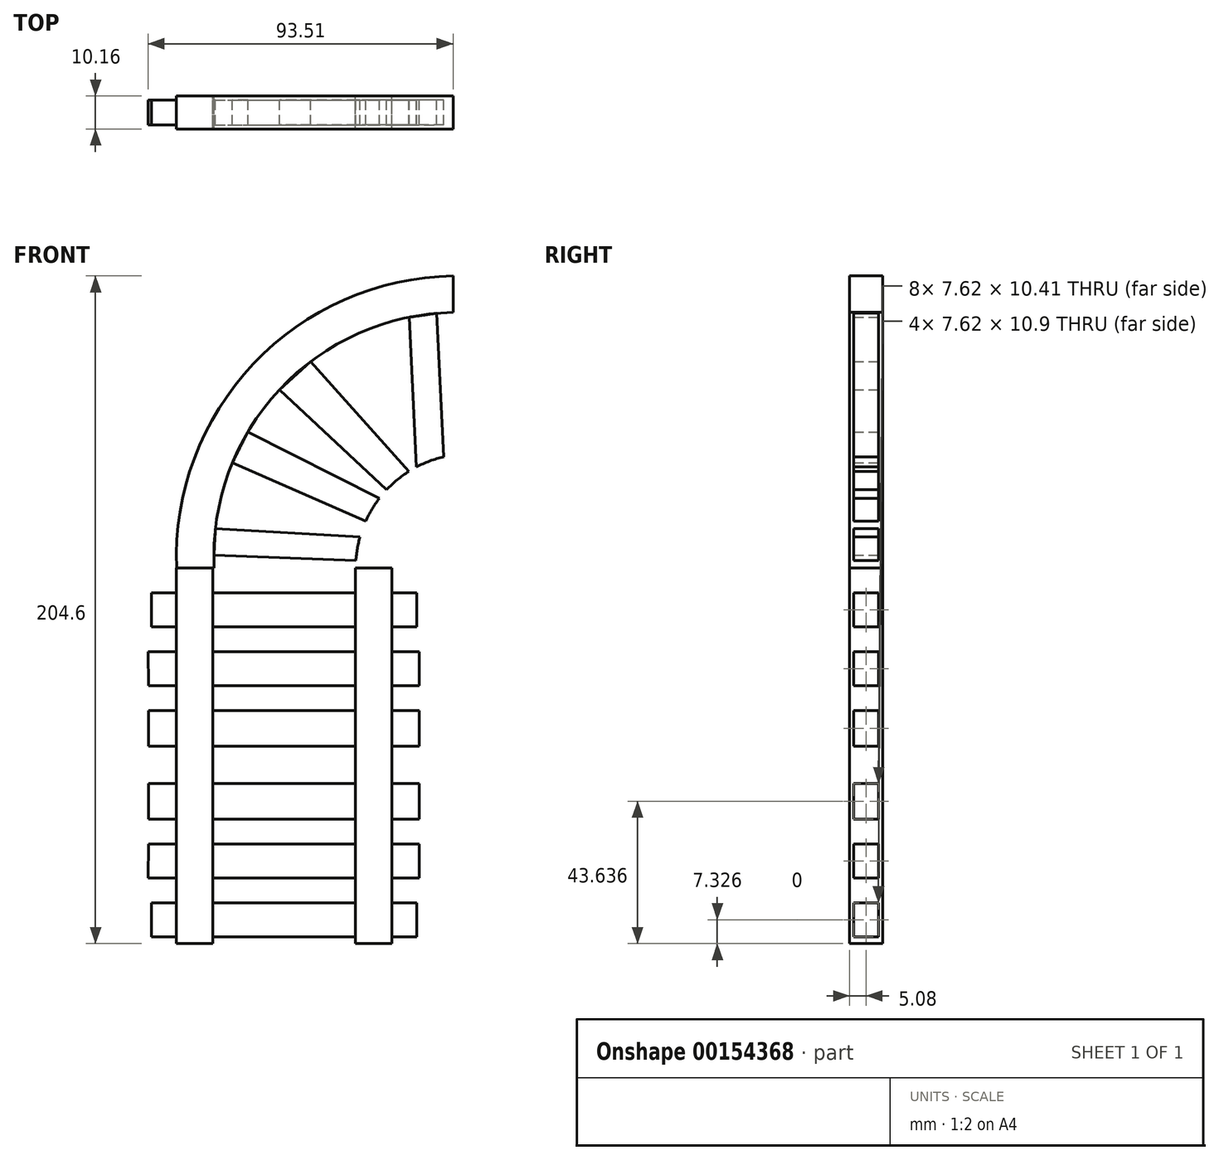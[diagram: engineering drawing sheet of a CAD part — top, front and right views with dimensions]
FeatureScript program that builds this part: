
annotation { "Feature Type Name" : "Feature", "Feature Type Description" : "" }
export const myFeature = defineFeature(function(context is Context, id is Id, definition is map)
    precondition{}
    {
        {
            var Q0;
            Q0=qCreatedBy(makeId("Front.planeOp"),FACE);
            var sketch = newSketch(context, id + "F0", { "sketchPlane" : qUnion([Q0])});
            skLineSegment(sketch, "E0", {"start": v(-21.84, 60.28) * mm, "end": v(-21.84, -54.78) * mm});
            skLineSegment(sketch, "E1", {"start": v(-21.84, -54.78) * mm, "end": v(-33.02, -54.78) * mm});
            skLineSegment(sketch, "E2", {"start": v(-33.02, -54.78) * mm, "end": v(-33.02, 60.28) * mm});
            skLineSegment(sketch, "E3", {"start": v(-33.02, 60.28) * mm, "end": v(-21.84, 60.28) * mm});
            skLineSegment(sketch, "E4.MirrorCS", {"start": v(21.84, 60.28) * mm, "end": v(21.84, -54.78) * mm});
            skLineSegment(sketch, "E5.MirrorCS", {"start": v(33.02, -54.78) * mm, "end": v(33.02, 60.28) * mm});
            skLineSegment(sketch, "E6.MirrorCS", {"start": v(33.02, 60.28) * mm, "end": v(21.84, 60.28) * mm});
            skLineSegment(sketch, "E7.MirrorCS", {"start": v(21.84, -54.78) * mm, "end": v(33.02, -54.78) * mm});
            skLineSegment(sketch, "E8", {"start": v(-40.64, 42.25) * mm, "end": v(40.64, 42.25) * mm});
            skLineSegment(sketch, "E9", {"start": v(40.64, 42.25) * mm, "end": v(40.64, 52.66) * mm});
            skLineSegment(sketch, "E10", {"start": v(40.64, 52.66) * mm, "end": v(-40.64, 52.66) * mm});
            skLineSegment(sketch, "E11", {"start": v(-40.64, 52.66) * mm, "end": v(-40.64, 42.25) * mm});
            skLineSegment(sketch, "E12", {"start": v(-41.74, 34.63) * mm, "end": v(41.35, 34.63) * mm});
            skLineSegment(sketch, "E13", {"start": v(41.35, 34.63) * mm, "end": v(41.35, 24.21) * mm});
            skLineSegment(sketch, "E14", {"start": v(41.35, 24.21) * mm, "end": v(-41.51, 24.21) * mm});
            skLineSegment(sketch, "E15", {"start": v(-41.51, 24.21) * mm, "end": v(-41.74, 34.63) * mm});
            skLineSegment(sketch, "E16", {"start": v(-33.02, 16.6) * mm, "end": v(-41.51, 16.6) * mm});
            skLineSegment(sketch, "E17", {"start": v(-41.51, 16.6) * mm, "end": v(-41.51, 5.7) * mm});
            skLineSegment(sketch, "E18", {"start": v(-41.51, 5.7) * mm, "end": v(41.4, 5.7) * mm});
            skLineSegment(sketch, "E19", {"start": v(41.4, 5.7) * mm, "end": v(41.4, 16.6) * mm});
            skLineSegment(sketch, "E20", {"start": v(-33.02, 16.6) * mm, "end": v(41.4, 16.6) * mm});
            skLineSegment(sketch, "E21.MirrorCS", {"start": v(-41.51, -5.7) * mm, "end": v(41.4, -5.7) * mm});
            skLineSegment(sketch, "E22.MirrorCS", {"start": v(-41.51, -16.6) * mm, "end": v(-41.51, -5.7) * mm});
            skLineSegment(sketch, "E23.MirrorCS", {"start": v(41.4, -5.7) * mm, "end": v(41.4, -16.6) * mm});
            skLineSegment(sketch, "E24.MirrorCS", {"start": v(-33.02, -16.6) * mm, "end": v(41.4, -16.6) * mm});
            skLineSegment(sketch, "E25.MirrorCS", {"start": v(-33.02, -16.6) * mm, "end": v(-41.51, -16.6) * mm});
            skLineSegment(sketch, "E26.MirrorCS", {"start": v(41.35, -24.21) * mm, "end": v(-41.51, -24.21) * mm});
            skLineSegment(sketch, "E27.MirrorCS", {"start": v(-41.74, -34.63) * mm, "end": v(41.35, -34.63) * mm});
            skLineSegment(sketch, "E28.MirrorCS", {"start": v(-41.51, -24.21) * mm, "end": v(-41.74, -34.63) * mm});
            skLineSegment(sketch, "E29.MirrorCS", {"start": v(41.35, -34.63) * mm, "end": v(41.35, -24.21) * mm});
            skLineSegment(sketch, "E30.MirrorCS", {"start": v(40.64, -42.25) * mm, "end": v(40.64, -52.66) * mm});
            skLineSegment(sketch, "E31.MirrorCS", {"start": v(40.64, -52.66) * mm, "end": v(-40.64, -52.66) * mm});
            skLineSegment(sketch, "E32.MirrorCS", {"start": v(-40.64, -42.25) * mm, "end": v(40.64, -42.25) * mm});
            skLineSegment(sketch, "E33.MirrorCS", {"start": v(-40.64, -52.66) * mm, "end": v(-40.64, -42.25) * mm});
            skSolve(sketch);
        }
        {
            var Q0;
            {var subQ0=sQuery(id+"F0.wireOp",EDGE,"E3");Q0=makeQuery(id+"F0.imprint","IMPRINT",FACE,{"disambiguationData":[TD([[makeQuery(id+"F0.imprint","IMPRINT",EDGE,{"derivedFrom":subQ0}),-1.0]])]});}
            var Q1;
            {var subQ0=sQuery(id+"F0.wireOp",EDGE,"E10");var subQ1=sQuery(id+"F0.wireOp",EDGE,"E0");var subQ2=makeQuery(id+"F0.imprint","INTERSECT",VERTEX,{"derivedFrom":[subQ1,subQ0]});Q1=makeQuery(id+"F0.imprint","IMPRINT",FACE,{"disambiguationData":[TD([[makeQuery(id+"F0.imprint","IMPRINT",EDGE,{"disambiguationData":[TD([[subQ2,-1.0]])],"derivedFrom":subQ1}),-1.0]])]});}
            var Q2;
            {var subQ0=sQuery(id+"F0.wireOp",EDGE,"E8");var subQ1=sQuery(id+"F0.wireOp",EDGE,"E0");var subQ2=makeQuery(id+"F0.imprint","INTERSECT",VERTEX,{"derivedFrom":[subQ1,subQ0]});Q2=makeQuery(id+"F0.imprint","IMPRINT",FACE,{"disambiguationData":[TD([[makeQuery(id+"F0.imprint","IMPRINT",EDGE,{"disambiguationData":[TD([[subQ2,-1.0]])],"derivedFrom":subQ1}),-1.0]])]});}
            var Q3;
            {var subQ0=sQuery(id+"F0.wireOp",EDGE,"E12");var subQ1=sQuery(id+"F0.wireOp",EDGE,"E0");var subQ2=makeQuery(id+"F0.imprint","INTERSECT",VERTEX,{"derivedFrom":[subQ1,subQ0]});Q3=makeQuery(id+"F0.imprint","IMPRINT",FACE,{"disambiguationData":[TD([[makeQuery(id+"F0.imprint","IMPRINT",EDGE,{"disambiguationData":[TD([[subQ2,-1.0]])],"derivedFrom":subQ1}),-1.0]])]});}
            var Q4;
            {var subQ0=sQuery(id+"F0.wireOp",EDGE,"E14");var subQ1=sQuery(id+"F0.wireOp",EDGE,"E0");var subQ2=makeQuery(id+"F0.imprint","INTERSECT",VERTEX,{"derivedFrom":[subQ1,subQ0]});Q4=makeQuery(id+"F0.imprint","IMPRINT",FACE,{"disambiguationData":[TD([[makeQuery(id+"F0.imprint","IMPRINT",EDGE,{"disambiguationData":[TD([[subQ2,-1.0]])],"derivedFrom":subQ1}),-1.0]])]});}
            var Q5;
            {var subQ0=sQuery(id+"F0.wireOp",EDGE,"E20");var subQ1=sQuery(id+"F0.wireOp",EDGE,"E0");var subQ2=makeQuery(id+"F0.imprint","INTERSECT",VERTEX,{"derivedFrom":[subQ1,subQ0]});Q5=makeQuery(id+"F0.imprint","IMPRINT",FACE,{"disambiguationData":[TD([[makeQuery(id+"F0.imprint","IMPRINT",EDGE,{"disambiguationData":[TD([[subQ2,-1.0]])],"derivedFrom":subQ1}),-1.0]])]});}
            var Q6;
            {var subQ0=sQuery(id+"F0.wireOp",EDGE,"E18");var subQ1=sQuery(id+"F0.wireOp",EDGE,"E0");var subQ2=makeQuery(id+"F0.imprint","INTERSECT",VERTEX,{"derivedFrom":[subQ1,subQ0]});Q6=makeQuery(id+"F0.imprint","IMPRINT",FACE,{"disambiguationData":[TD([[makeQuery(id+"F0.imprint","IMPRINT",EDGE,{"disambiguationData":[TD([[subQ2,-1.0]])],"derivedFrom":subQ1}),-1.0]])]});}
            var Q7;
            {var subQ0=sQuery(id+"F0.wireOp",EDGE,"E21.MirrorCS");var subQ1=sQuery(id+"F0.wireOp",EDGE,"E0");var subQ2=makeQuery(id+"F0.imprint","INTERSECT",VERTEX,{"derivedFrom":[subQ1,subQ0]});Q7=makeQuery(id+"F0.imprint","IMPRINT",FACE,{"disambiguationData":[TD([[makeQuery(id+"F0.imprint","IMPRINT",EDGE,{"disambiguationData":[TD([[subQ2,-1.0]])],"derivedFrom":subQ1}),-1.0]])]});}
            var Q8;
            {var subQ0=sQuery(id+"F0.wireOp",EDGE,"E24.MirrorCS");var subQ1=sQuery(id+"F0.wireOp",EDGE,"E0");var subQ2=makeQuery(id+"F0.imprint","INTERSECT",VERTEX,{"derivedFrom":[subQ1,subQ0]});Q8=makeQuery(id+"F0.imprint","IMPRINT",FACE,{"disambiguationData":[TD([[makeQuery(id+"F0.imprint","IMPRINT",EDGE,{"disambiguationData":[TD([[subQ2,-1.0]])],"derivedFrom":subQ1}),-1.0]])]});}
            var Q9;
            {var subQ0=sQuery(id+"F0.wireOp",EDGE,"E26.MirrorCS");var subQ1=sQuery(id+"F0.wireOp",EDGE,"E0");var subQ2=makeQuery(id+"F0.imprint","INTERSECT",VERTEX,{"derivedFrom":[subQ1,subQ0]});Q9=makeQuery(id+"F0.imprint","IMPRINT",FACE,{"disambiguationData":[TD([[makeQuery(id+"F0.imprint","IMPRINT",EDGE,{"disambiguationData":[TD([[subQ2,-1.0]])],"derivedFrom":subQ1}),-1.0]])]});}
            var Q10;
            {var subQ0=sQuery(id+"F0.wireOp",EDGE,"E27.MirrorCS");var subQ1=sQuery(id+"F0.wireOp",EDGE,"E0");var subQ2=makeQuery(id+"F0.imprint","INTERSECT",VERTEX,{"derivedFrom":[subQ1,subQ0]});Q10=makeQuery(id+"F0.imprint","IMPRINT",FACE,{"disambiguationData":[TD([[makeQuery(id+"F0.imprint","IMPRINT",EDGE,{"disambiguationData":[TD([[subQ2,-1.0]])],"derivedFrom":subQ1}),-1.0]])]});}
            var Q11;
            {var subQ0=sQuery(id+"F0.wireOp",EDGE,"E31.MirrorCS");var subQ1=sQuery(id+"F0.wireOp",EDGE,"E0");var subQ2=makeQuery(id+"F0.imprint","INTERSECT",VERTEX,{"derivedFrom":[subQ1,subQ0]});Q11=makeQuery(id+"F0.imprint","IMPRINT",FACE,{"disambiguationData":[TD([[makeQuery(id+"F0.imprint","IMPRINT",EDGE,{"disambiguationData":[TD([[subQ2,1.0]])],"derivedFrom":subQ1}),-1.0]])]});}
            var Q12;
            {var subQ0=sQuery(id+"F0.wireOp",EDGE,"E31.MirrorCS");var subQ1=sQuery(id+"F0.wireOp",EDGE,"E4.MirrorCS");var subQ2=makeQuery(id+"F0.imprint","INTERSECT",VERTEX,{"derivedFrom":[subQ1,subQ0]});Q12=makeQuery(id+"F0.imprint","IMPRINT",FACE,{"disambiguationData":[TD([[makeQuery(id+"F0.imprint","IMPRINT",EDGE,{"disambiguationData":[TD([[subQ2,1.0]])],"derivedFrom":subQ1}),1.0]])]});}
            var Q13;
            {var subQ0=sQuery(id+"F0.wireOp",EDGE,"E27.MirrorCS");var subQ1=sQuery(id+"F0.wireOp",EDGE,"E4.MirrorCS");var subQ2=makeQuery(id+"F0.imprint","INTERSECT",VERTEX,{"derivedFrom":[subQ1,subQ0]});Q13=makeQuery(id+"F0.imprint","IMPRINT",FACE,{"disambiguationData":[TD([[makeQuery(id+"F0.imprint","IMPRINT",EDGE,{"disambiguationData":[TD([[subQ2,-1.0]])],"derivedFrom":subQ1}),1.0]])]});}
            var Q14;
            {var subQ0=sQuery(id+"F0.wireOp",EDGE,"E26.MirrorCS");var subQ1=sQuery(id+"F0.wireOp",EDGE,"E4.MirrorCS");var subQ2=makeQuery(id+"F0.imprint","INTERSECT",VERTEX,{"derivedFrom":[subQ1,subQ0]});Q14=makeQuery(id+"F0.imprint","IMPRINT",FACE,{"disambiguationData":[TD([[makeQuery(id+"F0.imprint","IMPRINT",EDGE,{"disambiguationData":[TD([[subQ2,-1.0]])],"derivedFrom":subQ1}),1.0]])]});}
            var Q15;
            {var subQ0=sQuery(id+"F0.wireOp",EDGE,"E24.MirrorCS");var subQ1=sQuery(id+"F0.wireOp",EDGE,"E4.MirrorCS");var subQ2=makeQuery(id+"F0.imprint","INTERSECT",VERTEX,{"derivedFrom":[subQ1,subQ0]});Q15=makeQuery(id+"F0.imprint","IMPRINT",FACE,{"disambiguationData":[TD([[makeQuery(id+"F0.imprint","IMPRINT",EDGE,{"disambiguationData":[TD([[subQ2,-1.0]])],"derivedFrom":subQ1}),1.0]])]});}
            var Q16;
            {var subQ0=sQuery(id+"F0.wireOp",EDGE,"E21.MirrorCS");var subQ1=sQuery(id+"F0.wireOp",EDGE,"E4.MirrorCS");var subQ2=makeQuery(id+"F0.imprint","INTERSECT",VERTEX,{"derivedFrom":[subQ1,subQ0]});Q16=makeQuery(id+"F0.imprint","IMPRINT",FACE,{"disambiguationData":[TD([[makeQuery(id+"F0.imprint","IMPRINT",EDGE,{"disambiguationData":[TD([[subQ2,-1.0]])],"derivedFrom":subQ1}),1.0]])]});}
            var Q17;
            {var subQ0=sQuery(id+"F0.wireOp",EDGE,"E18");var subQ1=sQuery(id+"F0.wireOp",EDGE,"E4.MirrorCS");var subQ2=makeQuery(id+"F0.imprint","INTERSECT",VERTEX,{"derivedFrom":[subQ1,subQ0]});Q17=makeQuery(id+"F0.imprint","IMPRINT",FACE,{"disambiguationData":[TD([[makeQuery(id+"F0.imprint","IMPRINT",EDGE,{"disambiguationData":[TD([[subQ2,-1.0]])],"derivedFrom":subQ1}),1.0]])]});}
            var Q18;
            {var subQ0=sQuery(id+"F0.wireOp",EDGE,"E20");var subQ1=sQuery(id+"F0.wireOp",EDGE,"E4.MirrorCS");var subQ2=makeQuery(id+"F0.imprint","INTERSECT",VERTEX,{"derivedFrom":[subQ1,subQ0]});Q18=makeQuery(id+"F0.imprint","IMPRINT",FACE,{"disambiguationData":[TD([[makeQuery(id+"F0.imprint","IMPRINT",EDGE,{"disambiguationData":[TD([[subQ2,-1.0]])],"derivedFrom":subQ1}),1.0]])]});}
            var Q19;
            {var subQ0=sQuery(id+"F0.wireOp",EDGE,"E14");var subQ1=sQuery(id+"F0.wireOp",EDGE,"E4.MirrorCS");var subQ2=makeQuery(id+"F0.imprint","INTERSECT",VERTEX,{"derivedFrom":[subQ1,subQ0]});Q19=makeQuery(id+"F0.imprint","IMPRINT",FACE,{"disambiguationData":[TD([[makeQuery(id+"F0.imprint","IMPRINT",EDGE,{"disambiguationData":[TD([[subQ2,-1.0]])],"derivedFrom":subQ1}),1.0]])]});}
            var Q20;
            {var subQ0=sQuery(id+"F0.wireOp",EDGE,"E12");var subQ1=sQuery(id+"F0.wireOp",EDGE,"E4.MirrorCS");var subQ2=makeQuery(id+"F0.imprint","INTERSECT",VERTEX,{"derivedFrom":[subQ1,subQ0]});Q20=makeQuery(id+"F0.imprint","IMPRINT",FACE,{"disambiguationData":[TD([[makeQuery(id+"F0.imprint","IMPRINT",EDGE,{"disambiguationData":[TD([[subQ2,-1.0]])],"derivedFrom":subQ1}),1.0]])]});}
            var Q21;
            {var subQ0=sQuery(id+"F0.wireOp",EDGE,"E8");var subQ1=sQuery(id+"F0.wireOp",EDGE,"E4.MirrorCS");var subQ2=makeQuery(id+"F0.imprint","INTERSECT",VERTEX,{"derivedFrom":[subQ1,subQ0]});Q21=makeQuery(id+"F0.imprint","IMPRINT",FACE,{"disambiguationData":[TD([[makeQuery(id+"F0.imprint","IMPRINT",EDGE,{"disambiguationData":[TD([[subQ2,-1.0]])],"derivedFrom":subQ1}),1.0]])]});}
            var Q22;
            {var subQ0=sQuery(id+"F0.wireOp",EDGE,"E10");var subQ1=sQuery(id+"F0.wireOp",EDGE,"E4.MirrorCS");var subQ2=makeQuery(id+"F0.imprint","INTERSECT",VERTEX,{"derivedFrom":[subQ1,subQ0]});Q22=makeQuery(id+"F0.imprint","IMPRINT",FACE,{"disambiguationData":[TD([[makeQuery(id+"F0.imprint","IMPRINT",EDGE,{"disambiguationData":[TD([[subQ2,-1.0]])],"derivedFrom":subQ1}),1.0]])]});}
            var Q23;
            {var subQ0=sQuery(id+"F0.wireOp",EDGE,"E6.MirrorCS");Q23=makeQuery(id+"F0.imprint","IMPRINT",FACE,{"disambiguationData":[TD([[makeQuery(id+"F0.imprint","IMPRINT",EDGE,{"derivedFrom":subQ0}),1.0]])]});}
            var Q24;
            {var subQ0=sQuery(id+"F0.wireOp",EDGE,"E7.MirrorCS");Q24=makeQuery(id+"F0.imprint","IMPRINT",FACE,{"disambiguationData":[TD([[makeQuery(id+"F0.imprint","IMPRINT",EDGE,{"derivedFrom":subQ0}),1.0]])]});}
            var Q25;
            {var subQ0=sQuery(id+"F0.wireOp",EDGE,"E1");Q25=makeQuery(id+"F0.imprint","IMPRINT",FACE,{"disambiguationData":[TD([[makeQuery(id+"F0.imprint","IMPRINT",EDGE,{"derivedFrom":subQ0}),-1.0]])]});}
            extrude(context, id + "F1", {"entities" : qUnion([Q0, Q1, Q2, Q3, Q4, Q5, Q6, Q7, Q8, Q9, Q10, Q11, Q12, Q13, Q14, Q15, Q16, Q17, Q18, Q19, Q20, Q21, Q22, Q23, Q24, Q25]), "depth" : 5.08 * mm, "hasSecondDirection" : true, "secondDirectionOppositeDirection" : true, "secondDirectionDepth" : 5.08 * mm});
        }
        {
            var Q0;
            {var subQ0=sQuery(id+"F0.wireOp",EDGE,"E12");var subQ1=sQuery(id+"F0.wireOp",EDGE,"E0");var subQ2=makeQuery(id+"F0.imprint","INTERSECT",VERTEX,{"derivedFrom":[subQ1,subQ0]});Q0=makeQuery(id+"F0.imprint","IMPRINT",FACE,{"disambiguationData":[TD([[makeQuery(id+"F0.imprint","IMPRINT",EDGE,{"disambiguationData":[TD([[subQ2,-1.0]])],"derivedFrom":subQ1}),1.0]])]});}
            var Q1;
            {var subQ0=sQuery(id+"F0.wireOp",EDGE,"E10");var subQ1=sQuery(id+"F0.wireOp",EDGE,"E0");var subQ2=makeQuery(id+"F0.imprint","INTERSECT",VERTEX,{"derivedFrom":[subQ1,subQ0]});Q1=makeQuery(id+"F0.imprint","IMPRINT",FACE,{"disambiguationData":[TD([[makeQuery(id+"F0.imprint","IMPRINT",EDGE,{"disambiguationData":[TD([[subQ2,-1.0]])],"derivedFrom":subQ1}),1.0]])]});}
            var Q2;
            {var subQ5=sQuery(id+"F0.wireOp",EDGE,"E11");Q2=makeQuery(id+"F0.imprint","IMPRINT",FACE,{"disambiguationData":[TD([[makeQuery(id+"F0.imprint","IMPRINT",EDGE,{"derivedFrom":subQ5}),1.0]])]});}
            var Q3;
            {var subQ5=sQuery(id+"F0.wireOp",EDGE,"E15");Q3=makeQuery(id+"F0.imprint","IMPRINT",FACE,{"disambiguationData":[TD([[makeQuery(id+"F0.imprint","IMPRINT",EDGE,{"derivedFrom":subQ5}),-1.0]])]});}
            var Q4;
            {var subQ0=sQuery(id+"F0.wireOp",EDGE,"E16");Q4=makeQuery(id+"F0.imprint","IMPRINT",FACE,{"disambiguationData":[TD([[makeQuery(id+"F0.imprint","IMPRINT",EDGE,{"derivedFrom":subQ0}),1.0]])]});}
            var Q5;
            {var subQ4=sQuery(id+"F0.wireOp",EDGE,"E22.MirrorCS");Q5=makeQuery(id+"F0.imprint","IMPRINT",FACE,{"disambiguationData":[TD([[makeQuery(id+"F0.imprint","IMPRINT",EDGE,{"derivedFrom":subQ4}),-1.0]])]});}
            var Q6;
            {var subQ0=sQuery(id+"F0.wireOp",EDGE,"E21.MirrorCS");var subQ1=sQuery(id+"F0.wireOp",EDGE,"E0");var subQ2=makeQuery(id+"F0.imprint","INTERSECT",VERTEX,{"derivedFrom":[subQ1,subQ0]});Q6=makeQuery(id+"F0.imprint","IMPRINT",FACE,{"disambiguationData":[TD([[makeQuery(id+"F0.imprint","IMPRINT",EDGE,{"disambiguationData":[TD([[subQ2,-1.0]])],"derivedFrom":subQ1}),1.0]])]});}
            var Q7;
            {var subQ0=sQuery(id+"F0.wireOp",EDGE,"E20");var subQ1=sQuery(id+"F0.wireOp",EDGE,"E0");var subQ2=makeQuery(id+"F0.imprint","INTERSECT",VERTEX,{"derivedFrom":[subQ1,subQ0]});Q7=makeQuery(id+"F0.imprint","IMPRINT",FACE,{"disambiguationData":[TD([[makeQuery(id+"F0.imprint","IMPRINT",EDGE,{"disambiguationData":[TD([[subQ2,-1.0]])],"derivedFrom":subQ1}),1.0]])]});}
            var Q8;
            {var subQ0=sQuery(id+"F0.wireOp",EDGE,"E24.MirrorCS");var subQ1=sQuery(id+"F0.wireOp",EDGE,"E5.MirrorCS");var subQ2=makeQuery(id+"F0.imprint","INTERSECT",VERTEX,{"derivedFrom":[subQ1,subQ0]});Q8=makeQuery(id+"F0.imprint","IMPRINT",FACE,{"disambiguationData":[TD([[makeQuery(id+"F0.imprint","IMPRINT",EDGE,{"disambiguationData":[TD([[subQ2,-1.0]])],"derivedFrom":subQ1}),-1.0]])]});}
            var Q9;
            {var subQ0=sQuery(id+"F0.wireOp",EDGE,"E18");var subQ1=sQuery(id+"F0.wireOp",EDGE,"E5.MirrorCS");var subQ2=makeQuery(id+"F0.imprint","INTERSECT",VERTEX,{"derivedFrom":[subQ1,subQ0]});Q9=makeQuery(id+"F0.imprint","IMPRINT",FACE,{"disambiguationData":[TD([[makeQuery(id+"F0.imprint","IMPRINT",EDGE,{"disambiguationData":[TD([[subQ2,-1.0]])],"derivedFrom":subQ1}),-1.0]])]});}
            var Q10;
            {var subQ5=sQuery(id+"F0.wireOp",EDGE,"E13");Q10=makeQuery(id+"F0.imprint","IMPRINT",FACE,{"disambiguationData":[TD([[makeQuery(id+"F0.imprint","IMPRINT",EDGE,{"derivedFrom":subQ5}),-1.0]])]});}
            var Q11;
            {var subQ5=sQuery(id+"F0.wireOp",EDGE,"E9");Q11=makeQuery(id+"F0.imprint","IMPRINT",FACE,{"disambiguationData":[TD([[makeQuery(id+"F0.imprint","IMPRINT",EDGE,{"derivedFrom":subQ5}),1.0]])]});}
            var Q12;
            {var subQ5=sQuery(id+"F0.wireOp",EDGE,"E29.MirrorCS");Q12=makeQuery(id+"F0.imprint","IMPRINT",FACE,{"disambiguationData":[TD([[makeQuery(id+"F0.imprint","IMPRINT",EDGE,{"derivedFrom":subQ5}),1.0]])]});}
            var Q13;
            {var subQ5=sQuery(id+"F0.wireOp",EDGE,"E30.MirrorCS");Q13=makeQuery(id+"F0.imprint","IMPRINT",FACE,{"disambiguationData":[TD([[makeQuery(id+"F0.imprint","IMPRINT",EDGE,{"derivedFrom":subQ5}),-1.0]])]});}
            var Q14;
            {var subQ0=sQuery(id+"F0.wireOp",EDGE,"E31.MirrorCS");var subQ1=sQuery(id+"F0.wireOp",EDGE,"E0");var subQ2=makeQuery(id+"F0.imprint","INTERSECT",VERTEX,{"derivedFrom":[subQ1,subQ0]});Q14=makeQuery(id+"F0.imprint","IMPRINT",FACE,{"disambiguationData":[TD([[makeQuery(id+"F0.imprint","IMPRINT",EDGE,{"disambiguationData":[TD([[subQ2,1.0]])],"derivedFrom":subQ1}),1.0]])]});}
            var Q15;
            {var subQ0=sQuery(id+"F0.wireOp",EDGE,"E26.MirrorCS");var subQ1=sQuery(id+"F0.wireOp",EDGE,"E0");var subQ2=makeQuery(id+"F0.imprint","INTERSECT",VERTEX,{"derivedFrom":[subQ1,subQ0]});Q15=makeQuery(id+"F0.imprint","IMPRINT",FACE,{"disambiguationData":[TD([[makeQuery(id+"F0.imprint","IMPRINT",EDGE,{"disambiguationData":[TD([[subQ2,-1.0]])],"derivedFrom":subQ1}),1.0]])]});}
            var Q16;
            {var subQ5=sQuery(id+"F0.wireOp",EDGE,"E28.MirrorCS");Q16=makeQuery(id+"F0.imprint","IMPRINT",FACE,{"disambiguationData":[TD([[makeQuery(id+"F0.imprint","IMPRINT",EDGE,{"derivedFrom":subQ5}),1.0]])]});}
            var Q17;
            {var subQ5=sQuery(id+"F0.wireOp",EDGE,"E33.MirrorCS");Q17=makeQuery(id+"F0.imprint","IMPRINT",FACE,{"disambiguationData":[TD([[makeQuery(id+"F0.imprint","IMPRINT",EDGE,{"derivedFrom":subQ5}),-1.0]])]});}
            var Q18;
            Q18 = qSketchRegion(id + "F3", true);
            extrude(context, id + "F2", {"entities" : qUnion([Q0, Q1, Q2, Q3, Q4, Q5, Q6, Q7, Q8, Q9, Q10, Q11, Q12, Q13, Q14, Q15, Q16, Q17, Q18]), "operationType" : NewBodyOperationType.ADD, "depth" : 3.8 * mm, "hasSecondDirection" : true, "secondDirectionOppositeDirection" : true, "secondDirectionDepth" : 3.8 * mm});
        }
        {
            var Q0;
            Q0=qCreatedBy(makeId("Front.planeOp"),FACE);
            var sketch = newSketch(context, id + "F3", { "sketchPlane" : qUnion([Q0])});
            skLineSegment(sketch, "E34", {"start": v(51.77, 83.78) * mm, "end": v(51.77, 149.82) * mm});
            skArc(sketch, "E35", {"start": v(51.77, 149.82) * mm, "mid": v(-9.44, 122.88) * mm, "end": v(-32.96, 60.28) * mm});
            skLineSegment(sketch, "E36", {"start": v(51.77, 149.82) * mm, "end": v(51.77, 138.64) * mm});
            skLineSegment(sketch, "E37", {"start": v(51.77, 83.78) * mm, "end": v(51.77, 94.95) * mm});
            skArc(sketch, "E38", {"start": v(51.77, 138.64) * mm, "mid": v(-1.44, 114.97) * mm, "end": v(-21.43, 60.28) * mm});
            skArc(sketch, "E39", {"start": v(51.77, 83.78) * mm, "mid": v(37.26, 76.12) * mm, "end": v(33.02, 60.28) * mm});
            skArc(sketch, "E40", {"start": v(51.77, 94.95) * mm, "mid": v(25, 74.7) * mm, "end": v(27.58, 41.24) * mm});
            skLineSegment(sketch, "E41", {"start": v(-21.52, 64.26) * mm, "end": v(21.98, 62.59) * mm});
            skLineSegment(sketch, "E42", {"start": v(-21.06, 72.4) * mm, "end": v(23.24, 69.9) * mm});
            skLineSegment(sketch, "E43", {"start": v(-15.86, 92.57) * mm, "end": v(25, 74.7) * mm});
            skLineSegment(sketch, "E44", {"start": v(-11.13, 102.04) * mm, "end": v(29.15, 81.66) * mm});
            skLineSegment(sketch, "E45", {"start": v(33.02, 60.28) * mm, "end": v(21.9, 60.28) * mm});
            skLineSegment(sketch, "E46", {"start": v(-21.43, 60.28) * mm, "end": v(-32.96, 60.28) * mm});
            skLineSegment(sketch, "E47", {"start": v(48.84, 94.4) * mm, "end": v(46.72, 138.38) * mm});
            skLineSegment(sketch, "E48", {"start": v(31.4, 84.31) * mm, "end": v(-1.44, 114.97) * mm});
            skLineSegment(sketch, "E49", {"start": v(8.07, 123.54) * mm, "end": v(38.2, 89.91) * mm});
            skLineSegment(sketch, "E50", {"start": v(40.54, 91.27) * mm, "end": v(38.33, 137.18) * mm});
            skLineSegment(sketch, "E51", {"start": v(21.98, 62.59) * mm, "end": v(23.24, 69.9) * mm});
            skLineSegment(sketch, "E52", {"start": v(-21.06, 72.4) * mm, "end": v(-21.52, 64.26) * mm});
            skLineSegment(sketch, "E53", {"start": v(-11.13, 102.04) * mm, "end": v(-15.86, 92.57) * mm});
            skLineSegment(sketch, "E54", {"start": v(29.15, 81.66) * mm, "end": v(25, 74.7) * mm});
            skLineSegment(sketch, "E55", {"start": v(31.4, 84.31) * mm, "end": v(38.2, 89.91) * mm});
            skLineSegment(sketch, "E56", {"start": v(8.07, 123.54) * mm, "end": v(-1.44, 114.97) * mm});
            skLineSegment(sketch, "E57", {"start": v(38.33, 137.18) * mm, "end": v(46.72, 138.38) * mm});
            skLineSegment(sketch, "E58", {"start": v(40.54, 91.27) * mm, "end": v(48.84, 94.4) * mm});
            skSolve(sketch);
        }
        {
            var Q0;
            Q0=makeQuery(id+"F3.imprint","IMPRINT",FACE,{"disambiguationData":[TD([[makeQuery(id+"F3.imprint","IMPRINT",EDGE,{"derivedFrom":sQuery(id+"F3.wireOp",EDGE,"E35")}),1.0]])]});
            var Q1;
            {var subQ5=sQuery(id+"F3.wireOp",EDGE,"E37");Q1=makeQuery(id+"F3.imprint","IMPRINT",FACE,{"disambiguationData":[TD([[makeQuery(id+"F3.imprint","IMPRINT",EDGE,{"derivedFrom":subQ5}),1.0]])]});}
            extrude(context, id + "F4", {"entities" : qUnion([Q0, Q1]), "depth" : 5.08 * mm, "hasSecondDirection" : true, "secondDirectionOppositeDirection" : true, "secondDirectionDepth" : 5.08 * mm});
        }
        {
            var Q0;
            {var subQ1=sQuery(id+"F3.wireOp",EDGE,"E41");Q0=makeQuery(id+"F3.imprint","IMPRINT",FACE,{"disambiguationData":[TD([[makeQuery(id+"F3.imprint","IMPRINT",EDGE,{"derivedFrom":subQ1}),1.0]])]});}
            var Q1;
            {var subQ1=sQuery(id+"F3.wireOp",EDGE,"E43");Q1=makeQuery(id+"F3.imprint","IMPRINT",FACE,{"disambiguationData":[TD([[makeQuery(id+"F3.imprint","IMPRINT",EDGE,{"derivedFrom":subQ1}),1.0]])]});}
            var Q2;
            {var subQ1=sQuery(id+"F3.wireOp",EDGE,"E48");Q2=makeQuery(id+"F3.imprint","IMPRINT",FACE,{"disambiguationData":[TD([[makeQuery(id+"F3.imprint","IMPRINT",EDGE,{"derivedFrom":subQ1}),-1.0]])]});}
            var Q3;
            {var subQ1=sQuery(id+"F3.wireOp",EDGE,"E47");Q3=makeQuery(id+"F3.imprint","IMPRINT",FACE,{"disambiguationData":[TD([[makeQuery(id+"F3.imprint","IMPRINT",EDGE,{"derivedFrom":subQ1}),1.0]])]});}
            extrude(context, id + "F5", {"entities" : qUnion([Q0, Q1, Q2, Q3]), "operationType" : NewBodyOperationType.ADD, "depth" : 3.8 * mm, "hasSecondDirection" : true, "secondDirectionOppositeDirection" : true, "secondDirectionDepth" : 3.8 * mm});
        }
    });
